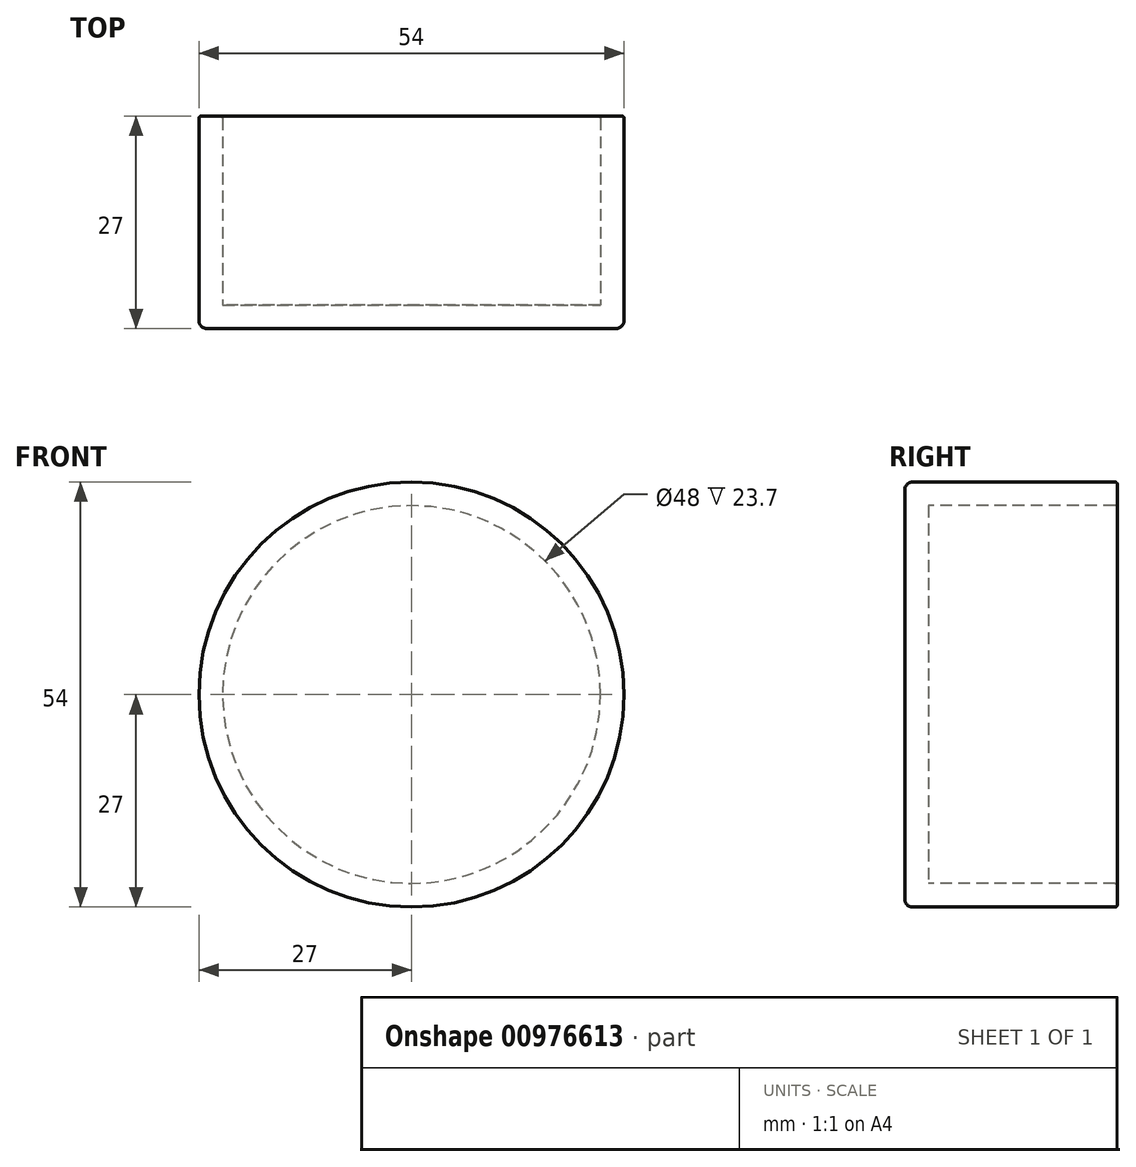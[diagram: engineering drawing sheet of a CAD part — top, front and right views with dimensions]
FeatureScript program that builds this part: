
annotation { "Feature Type Name" : "Feature", "Feature Type Description" : "" }
export const myFeature = defineFeature(function(context is Context, id is Id, definition is map)
    precondition{}
    {
        {
            var Q0;
            Q0=qCreatedBy(makeId("Front.planeOp"),FACE);
            var sketch = newSketch(context, id + "F0", { "sketchPlane" : qUnion([Q0])});
            skCircle(sketch, "E0", {"center": v(0, 0) * mm, "radius": 27 * mm});
            skSolve(sketch);
        }
        {
            var Q0;
            Q0=makeQuery(id+"F0.imprint","IMPRINT",FACE,{"disambiguationData":[TD([[makeQuery(id+"F0.imprint","IMPRINT",EDGE,{"derivedFrom":sQuery(id+"F0.wireOp",EDGE,"E0")}),1.0]])]});
            extrude(context, id + "F1", {"entities" : qUnion([Q0]), "depth" : 3 * mm, "offsetDistance" : 25 * mm});
        }
        {
            var Q0;
            Q0=makeQuery(id+"F1.opExtrude","CAP_FACE",FACE,{"disambiguationData":[OSD([sQuery(id+"F0.wireOp",EDGE,"E0")])],"isStart":true});
            var sketch = newSketch(context, id + "F2", { "sketchPlane" : qUnion([Q0])});
            skCircle(sketch, "E1", {"center": v(0, 0) * mm, "radius": 24 * mm});
            skSolve(sketch);
        }
        {
            var Q0;
            Q0=makeQuery(id+"F2.imprint","IMPRINT",FACE,{"disambiguationData":[TD([[makeQuery(id+"F2.imprint","IMPRINT",EDGE,{"derivedFrom":sQuery(id+"F2.wireOp",EDGE,"E1")}),-1.0]])]});
            extrude(context, id + "F3", {"entities" : qUnion([Q0]), "operationType" : NewBodyOperationType.ADD, "depth" : 24 * mm, "offsetDistance" : 25 * mm});
        }
        {
            var Q0;
            Q0=makeQuery(id+"F1.opExtrude","CAP_EDGE",EDGE,{"disambiguationData":[OSD([sQuery(id+"F0.wireOp",EDGE,"E0")])],"isStart":false});
            fillet(context, id + "F4", {"entities" : qUnion([Q0]), "radius" : 1 * mm, "tangentPropagation" : true, "allowEdgeOverflow" : false});
        }
        {
            var Q0;
            Q0=makeQuery(id+"F3.opExtrude","CAP_FACE",FACE,{"disambiguationData":[OSD([sQuery(id+"F0.wireOp",EDGE,"E0"),sQuery(id+"F2.wireOp",EDGE,"E1")])],"isStart":false});
            fillet(context, id + "F5", {"entities" : qUnion([Q0]), "radius" : .3 * mm, "tangentPropagation" : true, "allowEdgeOverflow" : false});
        }
    });
